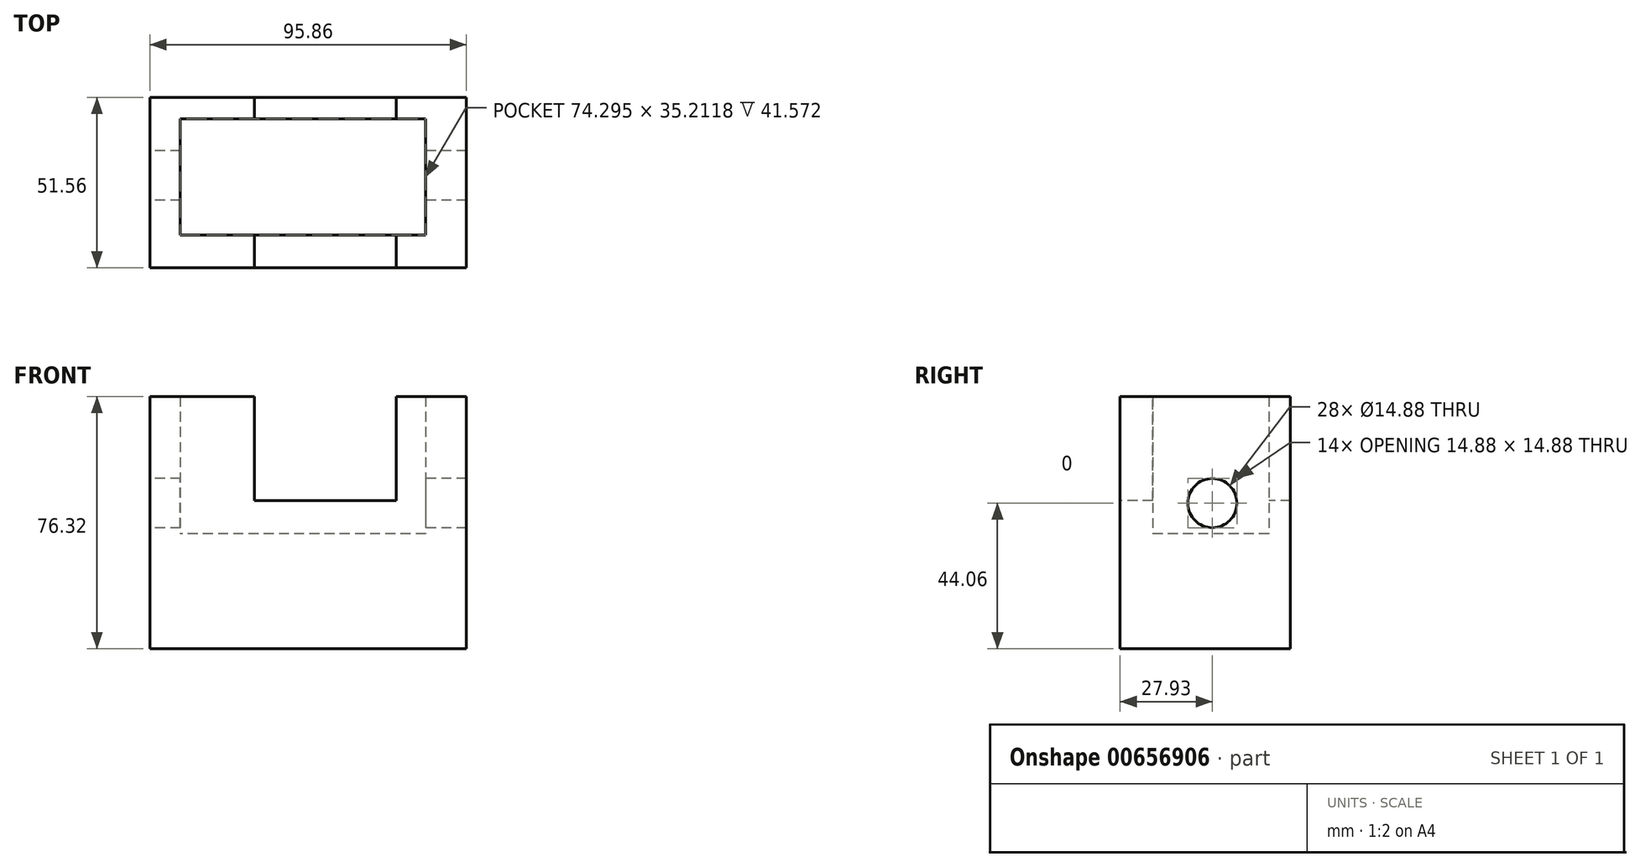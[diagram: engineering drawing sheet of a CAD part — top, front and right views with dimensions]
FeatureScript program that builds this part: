
annotation { "Feature Type Name" : "Feature", "Feature Type Description" : "" }
export const myFeature = defineFeature(function(context is Context, id is Id, definition is map)
    precondition{}
    {
        {
            var Q0;
            Q0=qCreatedBy(makeId("Front.planeOp"),FACE);
            var sketch = newSketch(context, id + "F0", { "sketchPlane" : qUnion([Q0])});
            skLineSegment(sketch, "E0", {"start": v(-49.31, 41.57) * mm, "end": v(-49.31, -34.75) * mm});
            skLineSegment(sketch, "E1", {"start": v(-49.31, -34.75) * mm, "end": v(46.55, -34.75) * mm});
            skLineSegment(sketch, "E2", {"start": v(46.55, -34.75) * mm, "end": v(46.55, 41.57) * mm});
            skLineSegment(sketch, "E3", {"start": v(46.55, 41.57) * mm, "end": v(-49.31, 41.57) * mm});
            skSolve(sketch);
        }
        {
            var Q0;
            Q0=makeQuery(id+"F0.imprint","IMPRINT",FACE,{"disambiguationData":[TD([[makeQuery(id+"F0.imprint","IMPRINT",EDGE,{"derivedFrom":sQuery(id+"F0.wireOp",EDGE,"E0")}),1.0]])]});
            extrude(context, id + "F1", {"entities" : qUnion([Q0]), "oppositeDirection" : true, "depth" : 51.56 * mm, "offsetDistance" : 25.4 * mm});
        }
        {
            var Q0;
            Q0=qCreatedBy(makeId("Top.planeOp"),FACE);
            var sketch = newSketch(context, id + "F2", { "sketchPlane" : qUnion([Q0])});
            skLineSegment(sketch, "E4", {"start": v(-40.1, 45.07) * mm, "end": v(-40.1, 9.86) * mm});
            skLineSegment(sketch, "E5", {"start": v(-40.1, 9.86) * mm, "end": v(34.2, 9.86) * mm});
            skLineSegment(sketch, "E6", {"start": v(34.2, 9.86) * mm, "end": v(34.2, 45.07) * mm});
            skLineSegment(sketch, "E7", {"start": v(34.2, 45.07) * mm, "end": v(-40.1, 45.07) * mm});
            skSolve(sketch);
        }
        {
            var Q0;
            Q0 = qSketchRegion(id + "F2", true);
            extrude(context, id + "F3", {"entities" : qUnion([Q0]), "operationType" : NewBodyOperationType.REMOVE, "depth" : 73.15 * mm, "offsetDistance" : 25.4 * mm});
        }
        {
            var Q0;
            Q0=qCreatedBy(makeId("Right.planeOp"),FACE);
            var sketch = newSketch(context, id + "F4", { "sketchPlane" : qUnion([Q0])});
            skCircle(sketch, "E8", {"center": v(27.93, 9.3) * mm, "radius": 7.44 * mm});
            skSolve(sketch);
        }
        {
            var Q0;
            Q0 = qSketchRegion(id + "F4", true);
            extrude(context, id + "F5", {"entities" : qUnion([Q0]), "operationType" : NewBodyOperationType.REMOVE, "endBound" : BoundingType.SYMMETRIC, "depth" : 106.68 * mm, "offsetDistance" : 25.4 * mm});
        }
        {
            var Q0;
            Q0=makeQuery(id+"F1.opExtrude","CAP_FACE",FACE,{"disambiguationData":[OSD([sQuery(id+"F0.wireOp",EDGE,"E0"),sQuery(id+"F0.wireOp",EDGE,"E1"),sQuery(id+"F0.wireOp",EDGE,"E2"),sQuery(id+"F0.wireOp",EDGE,"E3")])],"isStart":true});
            var sketch = newSketch(context, id + "F6", { "sketchPlane" : qUnion([Q0])});
            skLineSegment(sketch, "E9", {"start": v(-17.6, 41.57) * mm, "end": v(-17.6, 10.05) * mm});
            skLineSegment(sketch, "E10", {"start": v(-17.6, 10.05) * mm, "end": v(25.35, 10.05) * mm});
            skLineSegment(sketch, "E11", {"start": v(25.35, 10.05) * mm, "end": v(25.35, 41.57) * mm});
            skLineSegment(sketch, "E12", {"start": v(25.35, 41.57) * mm, "end": v(-17.6, 41.57) * mm});
            skLineSegment(sketch, "E13", {"start": v(-17.6, 41.57) * mm, "end": v(25.35, 41.57) * mm});
            skSolve(sketch);
        }
        {
            var Q0;
            Q0 = qSketchRegion(id + "F6", true);
            extrude(context, id + "F7", {"entities" : qUnion([Q0]), "operationType" : NewBodyOperationType.REMOVE, "oppositeDirection" : true, "depth" : 57.9 * mm, "offsetDistance" : 25.4 * mm});
        }
    });
